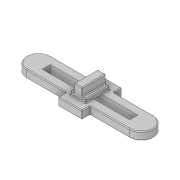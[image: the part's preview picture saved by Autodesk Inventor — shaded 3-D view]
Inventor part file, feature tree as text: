
AUTODESK INVENTOR PART (.ipt)
format: ipt  version: 2017 (Build 210142000, 142)  size: 246,272 bytes
history: native  units: in
note: dims shown in document units (in); Inventor stores cm internally (conversion verified against a paired STEP export)
features: fillet x7, extrude x2, sketch x2
ambient origin geometry x8: Origin, YZ Plane, XZ Plane, XY Plane, X Axis, Y Axis, Z Axis, Center Point
bodies: Solid1 (feature_tree)
feature tree (11):
  extrude  "Extrusion1"  Depth=0.59in
  extrude  "Extrusion2"  Depth=4.35in
  fillet  "Fillet1"  Radius=0.4in
  fillet  "Fillet2"  Radius=0.4in
  fillet  "Fillet3"  Radius=0.4in
  fillet  "Fillet4"  Radius=0.78in
  fillet  "Fillet5"  Radius=0.4in
  fillet  "Fillet6"  Radius=0.4in
  fillet  "Fillet7"  Radius=0.19in
  sketch  "Sketch1"  dims[d0=5.11in d1=0.59in]
  sketch  "Sketch2"  dims[d2=1.18in d3=4.35in d4=0.4in d5=0.4in d6=0.4in d7=0.0in d8=0.78in d9=0.4in d10=0.4in d11=0.19in d12=0.2in d13=1.18in d14=0.0in d15=0.04in d16=0.04in d17=0.04in d18=0.04in d19=0.04in d20=0.04in d21=0.04in]
